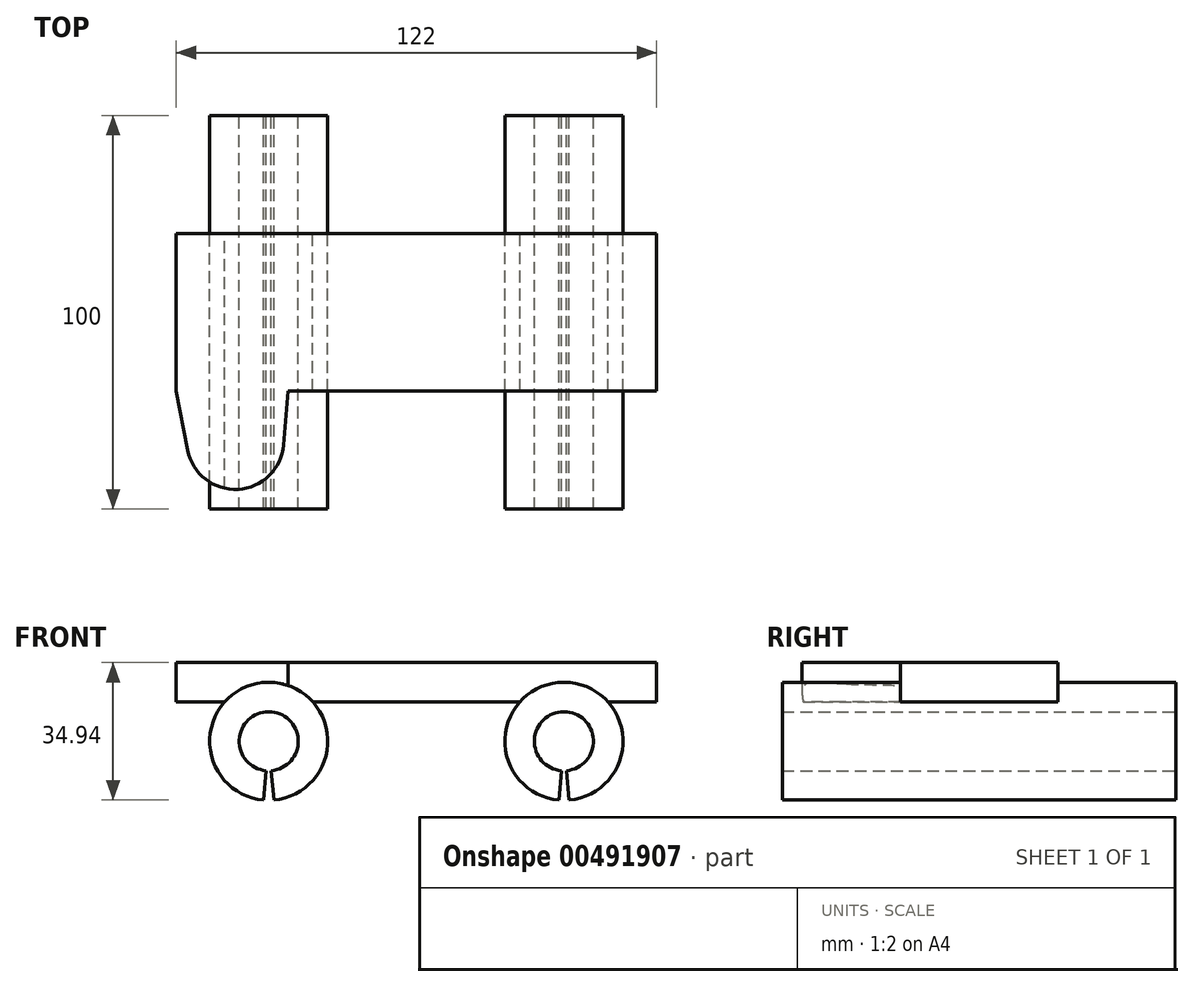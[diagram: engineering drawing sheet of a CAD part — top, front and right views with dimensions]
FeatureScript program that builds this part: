
annotation { "Feature Type Name" : "Feature", "Feature Type Description" : "" }
export const myFeature = defineFeature(function(context is Context, id is Id, definition is map)
    precondition{}
    {
        {
            var Q0;
            Q0=qCreatedBy(makeId("Top.planeOp"),FACE);
            var sketch = newSketch(context, id + "F0", { "sketchPlane" : qUnion([Q0])});
            skLineSegment(sketch, "E0.bottom", {"start": v(61, -20) * mm, "end": v(-61, -20) * mm});
            skLineSegment(sketch, "E0.top", {"start": v(61, 20) * mm, "end": v(-61, 20) * mm});
            skLineSegment(sketch, "E0.left", {"start": v(61, -20) * mm, "end": v(61, 20) * mm});
            skLineSegment(sketch, "E0.right", {"start": v(-61, -20) * mm, "end": v(-61, 20) * mm});
            skPoint(sketch, "E0.middle", {"position": v(0, 0) * mm});
            skLineSegment(sketch, "E1", {"start": v(-61, -20) * mm, "end": v(-31, -20) * mm, "construction": true});
            skLineSegment(sketch, "E2", {"start": v(-46, -20) * mm, "end": v(-46, -32.7) * mm, "construction": true});
            skCircle(sketch, "E3", {"center": v(-46, -32.7) * mm, "radius": 12.3 * mm, "construction": true});
            skLineSegment(sketch, "E4", {"start": v(-33.74, -33.7) * mm, "end": v(-32.63, -20) * mm});
            skLineSegment(sketch, "E5", {"start": v(-61, -20) * mm, "end": v(-58.07, -35.05) * mm});
            skArc(sketch, "E6", {"start": v(-58.07, -35.05) * mm, "mid": v(-45.32, -44.98) * mm, "end": v(-33.74, -33.7) * mm});
            skCircle(sketch, "E7", {"center": v(12, 0) * mm, "radius": 4 * mm, "construction": true});
            skSolve(sketch);
        }
        {
            var Q0;
            Q0 = qSketchRegion(id + "F0", true);
            extrude(context, id + "F1", {"entities" : qUnion([Q0]), "depth" : 10 * mm});
        }
        {
            var Q0;
            Q0=qCreatedBy(makeId("Front.planeOp"),FACE);
            var sketch = newSketch(context, id + "F2", { "sketchPlane" : qUnion([Q0])});
            skLineSegment(sketch, "E8", {"start": v(37.5, -10) * mm, "end": v(-37.5, -10) * mm, "construction": true});
            skCircle(sketch, "E9", {"center": v(37.5, -10) * mm, "radius": 7.5 * mm, "construction": true});
            skLineSegment(sketch, "E10", {"start": v(0, 0) * mm, "end": v(0, -10) * mm, "construction": true});
            skCircle(sketch, "E11", {"center": v(37.5, -10) * mm, "radius": 15 * mm, "construction": true});
            skLineSegment(sketch, "E12", {"start": v(37.5, -17.5) * mm, "end": v(37.5, -25) * mm, "construction": true});
            skLineSegment(sketch, "E13", {"start": v(37.5, -10) * mm, "end": v(38.15, -17.47) * mm, "construction": true});
            skLineSegment(sketch, "E14", {"start": v(37.5, -10) * mm, "end": v(36.85, -17.47) * mm, "construction": true});
            skLineSegment(sketch, "E15", {"start": v(38.15, -17.47) * mm, "end": v(38.8, -24.94) * mm});
            skLineSegment(sketch, "E16", {"start": v(36.85, -17.47) * mm, "end": v(36.2, -24.94) * mm});
            skArc(sketch, "E17", {"start": v(38.15, -17.47) * mm, "mid": v(37.5, -2.5) * mm, "end": v(36.85, -17.47) * mm});
            skArc(sketch, "E18", {"start": v(36.2, -24.94) * mm, "mid": v(37.5, 5) * mm, "end": v(38.8, -24.94) * mm});
            skLineSegment(sketch, "E19.MirrorCS", {"start": v(-38.15, -17.47) * mm, "end": v(-38.8, -24.94) * mm});
            skLineSegment(sketch, "E20.MirrorCS", {"start": v(-36.85, -17.47) * mm, "end": v(-36.2, -24.94) * mm});
            skCircle(sketch, "E21.MirrorC", {"center": v(-37.5, -10) * mm, "radius": 15 * mm, "construction": true});
            skArc(sketch, "E22.MirrorCS", {"start": v(-36.2, -24.94) * mm, "mid": v(-37.5, 5) * mm, "end": v(-38.8, -24.94) * mm});
            skArc(sketch, "E23.MirrorCS", {"start": v(-38.15, -17.47) * mm, "mid": v(-37.5, -2.5) * mm, "end": v(-36.85, -17.47) * mm});
            skSolve(sketch);
        }
        {
            var Q0;
            Q0 = qSketchRegion(id + "F2", true);
            extrude(context, id + "F3", {"entities" : qUnion([Q0]), "operationType" : NewBodyOperationType.ADD, "endBound" : BoundingType.SYMMETRIC, "depth" : 100 * mm, "offsetDistance" : 25 * mm});
        }
    });
